# Revit family: Hitachi_RAS-70YHA_RAS-80YHA_VER2_0813
name_source: partatom
category: Mechanical Equipment
revit_build: Autodesk Revit 2013 (Build: 20120221_2030(x64)
units: mm (PartAtom-declared; Revit-internal decimal feet)

## types (2) — shared parameters
Dehumidifying Capacity = 4.8 l/h
Depth = 245 mm  [stored 0.803806 ft]
Energy Star = Yes
Heating Range (kW) = 1.5 kW to 9.7 kW
Height = 333 mm  [stored 1.09252 ft]
Manufacturer = Hitachi
Pip Connection Size - Liquid = 6.40 mm
Pipe Connection Size - Gas = 15.90 mm
Pipe Height (max.) = 20m
Pipe Length (min./max.) = 3m to 30m
Weight (kg) = 16
Width = 1150 mm

## per-type parameters (varying)
| type | Cooling Capacity | Cooling Range (kW) | Description | Heating Capacity | Model - Outdoor | URL |
| RAS-80YHA3 | 8 kW | 1.5 kW to 8.5 kW | Hitachi Wall Mounted 8.0kW Heatpump RAS-80YHA3 | 9 kW | RAC-80YHA3 | http://www.temperzone.biz |
| RAS-70YHA3 | 7 kW | 1.5 kW to 8.3 kW | Hitachi Wall Mounted 7.0kW Heatpump RAS-70YHA3 | 8 kW | RAC-70YHA3 | www.temperzone.biz |

note: column(s) folded — value = type name in every type: Model

note: [stored X ft] marks values corroborated as IEEE doubles in the binary element streams (Revit-internal decimal feet)

## geometry (parser evidence)
native form markers: Blend x4, Sweep x3
no freeform markers — native parametric forms only
